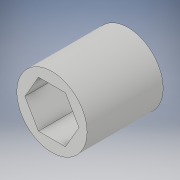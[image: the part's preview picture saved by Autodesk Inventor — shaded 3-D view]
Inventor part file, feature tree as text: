
AUTODESK INVENTOR PART (.ipt)
format: ipt  version: 2018 (Build 220112000, 112)  size: 101,376 bytes
history: native  units: in
note: dims shown in document units (in); Inventor stores cm internally (conversion verified against a paired STEP export)
features: extrude x1, sketch x1
ambient origin geometry x8: Origin, YZ Plane, XZ Plane, XY Plane, X Axis, Y Axis, Z Axis, Center Point
bodies: Solid1 (feature_tree)
feature tree (2):
  extrude  "Extrusion1"  Depth=0.8125in
  sketch  "Sketch1"  dims[d0=0.5in d1=0.75in d2=0.8125in d3=0.0in]
